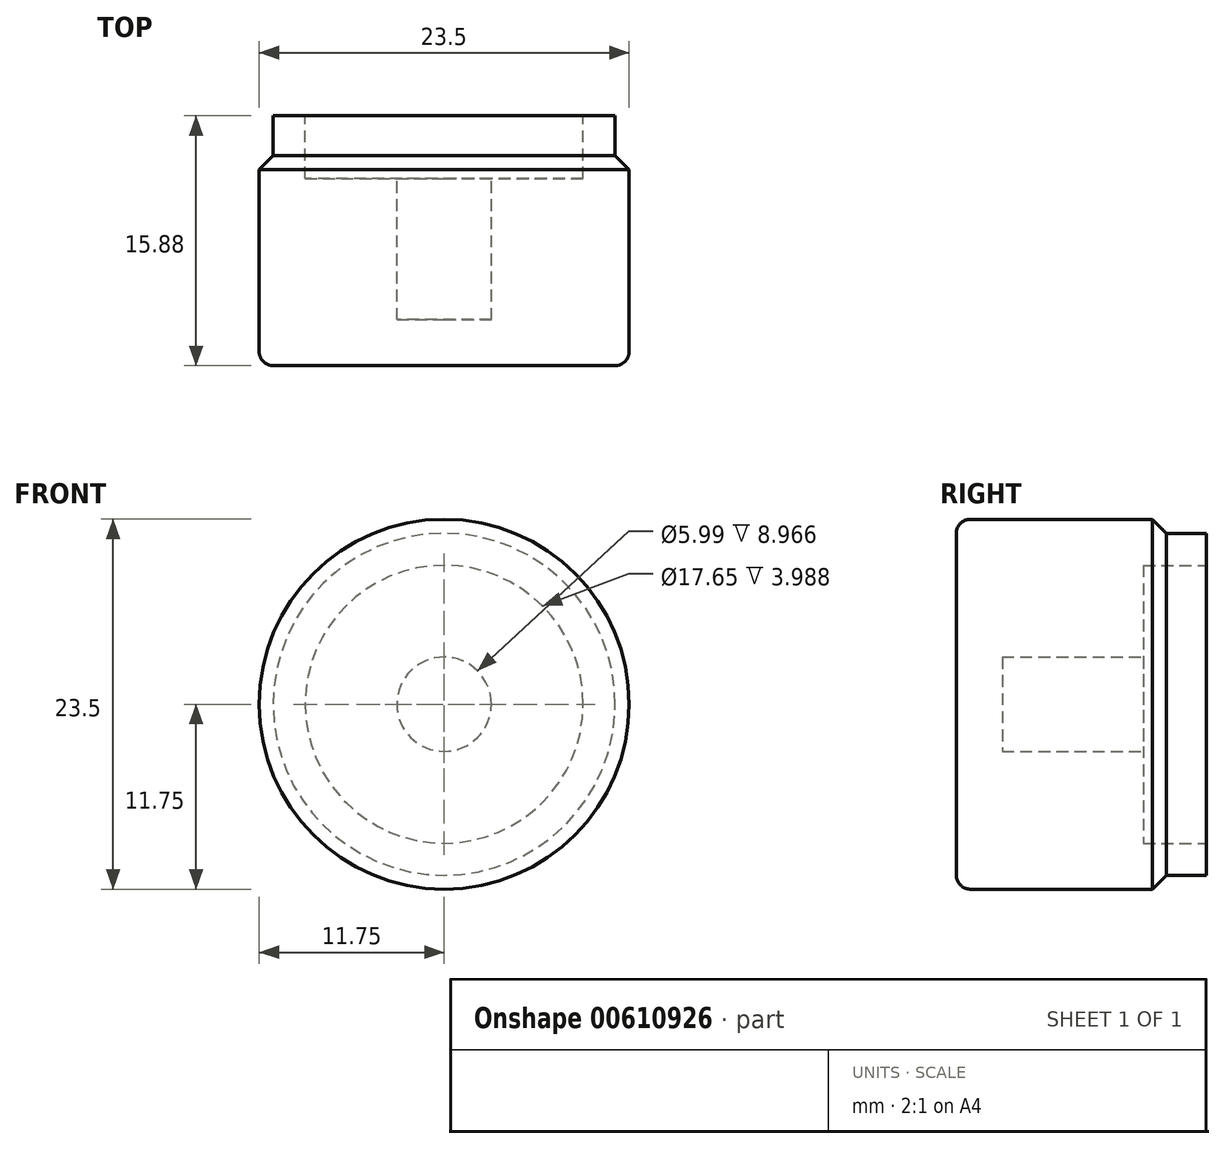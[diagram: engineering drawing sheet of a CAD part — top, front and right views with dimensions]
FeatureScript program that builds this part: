
annotation { "Feature Type Name" : "Feature", "Feature Type Description" : "" }
export const myFeature = defineFeature(function(context is Context, id is Id, definition is map)
    precondition{}
    {
        {
            var Q0;
            Q0=qCreatedBy(makeId("Right.planeOp"),FACE);
            var sketch = newSketch(context, id + "F0", { "sketchPlane" : qUnion([Q0])});
            skLineSegment(sketch, "E0", {"start": v(0, 0) * mm, "end": v(-12.95, 0) * mm, "construction": true});
            skLineSegment(sketch, "E1", {"start": v(-12.95, 0) * mm, "end": v(-12.95, 3) * mm});
            skLineSegment(sketch, "E2", {"start": v(-12.95, 3) * mm, "end": v(-3.99, 3) * mm});
            skLineSegment(sketch, "E3", {"start": v(-3.99, 3) * mm, "end": v(-3.99, 8.83) * mm});
            skLineSegment(sketch, "E4", {"start": v(-3.99, 8.83) * mm, "end": v(0, 8.83) * mm});
            skLineSegment(sketch, "E5", {"start": v(0, 8.83) * mm, "end": v(0, 10.86) * mm});
            skLineSegment(sketch, "E6", {"start": v(-3.43, 11.75) * mm, "end": v(-14.99, 11.75) * mm});
            skLineSegment(sketch, "E7", {"start": v(-12.95, 0) * mm, "end": v(-15.88, 0) * mm});
            skLineSegment(sketch, "E8", {"start": v(-15.88, 0) * mm, "end": v(-15.88, 10.86) * mm});
            skArc(sketch, "E9", {"start": v(-14.99, 11.75) * mm, "mid": v(-15.61, 11.49) * mm, "end": v(-15.88, 10.86) * mm});
            skLineSegment(sketch, "E10", {"start": v(-3.43, 11.75) * mm, "end": v(-2.54, 10.86) * mm});
            skLineSegment(sketch, "E11", {"start": v(-2.54, 10.86) * mm, "end": v(0, 10.86) * mm});
            skSolve(sketch);
        }
        {
            var Q0;
            Q0 = qSketchRegion(id + "F0", true);
            var Q1;
            Q1=sQuery(id+"F0.wireOp",EDGE,"E0");
            revolve(context, id + "F1", {"surfaceOperationType" : NewSurfaceOperationType.NEW, "entities" : qUnion([Q0]), "axis" : qUnion([Q1]), "revolveType" : RevolveType.FULL});
        }
    });
